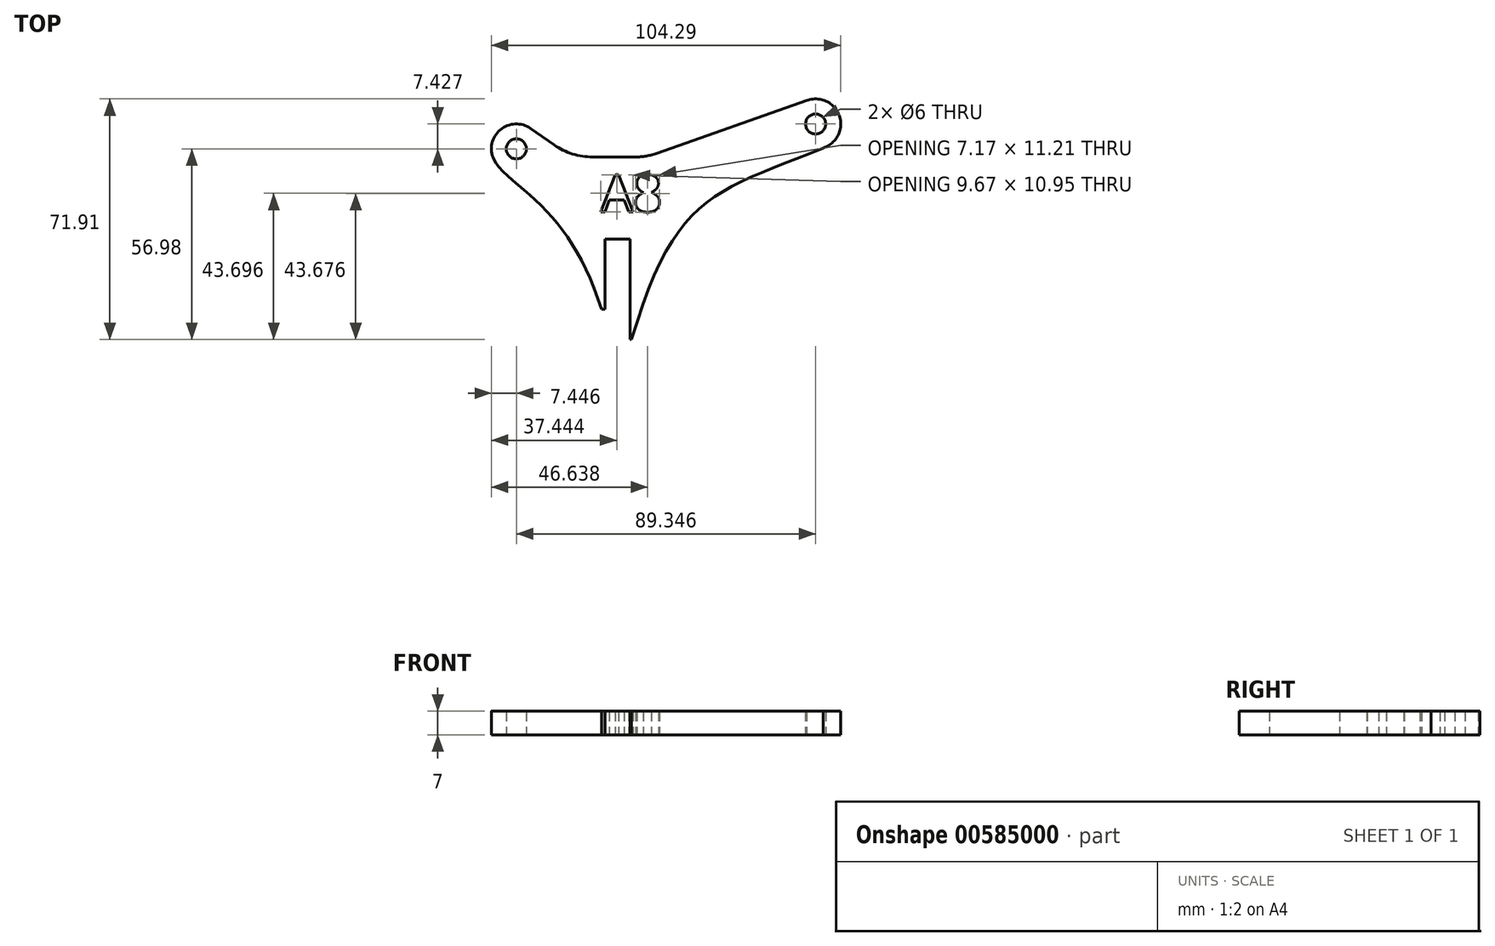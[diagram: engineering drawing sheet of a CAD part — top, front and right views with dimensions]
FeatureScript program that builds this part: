
annotation { "Feature Type Name" : "Feature", "Feature Type Description" : "" }
export const myFeature = defineFeature(function(context is Context, id is Id, definition is map)
    precondition{}
    {
        {
            var Q0;
            Q0=qCreatedBy(makeId("Top.planeOp"),FACE);
            var sketch = newSketch(context, id + "F0", { "sketchPlane" : qUnion([Q0])});
            skLineSegment(sketch, "E0", {"start": v(-34.62, 42.23) * mm, "end": v(65.38, 42.2) * mm, "construction": true});
            skLineSegment(sketch, "E1.left", {"start": v(2.5, -5) * mm, "end": v(2.5, 7.8) * mm});
            skLineSegment(sketch, "E1.right", {"start": v(10, -15) * mm, "end": v(10, 7.8) * mm});
            skPoint(sketch, "E1.middle", {"position": v(0, 0) * mm});
            skArc(sketch, "E2", {"start": v(67.67, 35.06) * mm, "mid": v(72.45, 44.7) * mm, "end": v(62.67, 49.2) * mm});
            skLineSegment(sketch, "E3", {"start": v(-34.62, 42.23) * mm, "end": v(15.38, 42.22) * mm, "construction": true});
            skLineSegment(sketch, "E4", {"start": v(-19.7, 40.88) * mm, "end": v(-12.67, 35.97) * mm});
            skLineSegment(sketch, "E5", {"start": v(18.13, 33.5) * mm, "end": v(62.67, 49.2) * mm});
            skLineSegment(sketch, "E6", {"start": v(-1.21, 32.36) * mm, "end": v(11.48, 32.36) * mm});
            skPoint(sketch, "E7.orphan", {"position": v(0, 27.1) * mm});
            skLineSegment(sketch, "E8", {"start": v(15.38, 42.22) * mm, "end": v(15.38, 24.58) * mm, "construction": true});
            skLineSegment(sketch, "E9", {"start": v(-34.62, 42.23) * mm, "end": v(-1.08, 18.78) * mm, "construction": true});
            skLineSegment(sketch, "E10", {"start": v(65.38, 42.2) * mm, "end": v(-1.08, 18.78) * mm, "construction": true});
            skCircle(sketch, "E11", {"center": v(65.38, 42.2) * mm, "radius": 3 * mm});
            skCircle(sketch, "E12", {"center": v(-23.96, 34.78) * mm, "radius": 3 * mm});
            skLineSegment(sketch, "E13", {"start": v(-23.96, 34.78) * mm, "end": v(90.1, 34.76) * mm, "construction": true});
            skLineSegment(sketch, "E14", {"start": v(-13.3, 27.33) * mm, "end": v(81.32, 27.31) * mm, "construction": true});
            skLineSegment(sketch, "E15", {"start": v(2.5, 7.8) * mm, "end": v(10, 7.8) * mm});
            skLineSegment(sketch, "E16", {"start": v(2.5, -5) * mm, "end": v(2.5, -13.17) * mm});
            skLineSegment(sketch, "E17", {"start": v(10, -15) * mm, "end": v(10, -22.2) * mm});
            skFitSpline(sketch, "E18", {"points": [v(10, -23.7) * mm, v(67.67, 35.06) * mm], "startDerivative": vector(38.94, 135.29) * mm, "endDerivative": vector(98.1, 40.08) * mm});
            skText(sketch, "E19", { "text": "A8", "fontName": "OpenSans-Regular.ttf"});
            skArc(sketch, "E20", {"start": v(-19.7, 40.88) * mm, "mid": v(-28.76, 40.47) * mm, "end": v(-30.7, 31.6) * mm});
            skPoint(sketch, "E21.0.visualSharp", {"position": v(-7.51, 32.36) * mm});
            skArc(sketch, "E21.0.filletArc", {"start": v(-12.67, 35.97) * mm, "mid": v(-7.22, 33.28) * mm, "end": v(-1.21, 32.36) * mm});
            skPoint(sketch, "E22.0.visualSharp", {"position": v(14.9, 32.36) * mm});
            skArc(sketch, "E22.0.filletArc", {"start": v(11.48, 32.36) * mm, "mid": v(14.85, 32.65) * mm, "end": v(18.13, 33.5) * mm});
            skLineSegment(sketch, "E23", {"start": v(2.5, -13.17) * mm, "end": v(1.5, -13.17) * mm});
            skLineSegment(sketch, "E24", {"start": v(10, -22.2) * mm, "end": v(10.44, -22.2) * mm});
            skFitSpline(sketch, "E25", {"points": [v(1.5, -13.17) * mm, v(-17.31, 18.56) * mm, v(-30.7, 31.6) * mm], "startDerivative": vector(-25.05, 77.18) * mm, "endDerivative": vector(-12.43, 26.26) * mm});
            const initialGuessF0  = {"E19": [0.0012, 0.01602, 1, 0, 0.011]};
            skSetInitialGuess(sketch, initialGuessF0);
            skSolve(sketch);
        }
        {
            var Q0;
            Q0=makeQuery(id+"F0.imprint","IMPRINT",FACE,{"disambiguationData":[TD([[makeQuery(id+"F0.imprint","IMPRINT",EDGE,{"derivedFrom":sQuery(id+"F0.wireOp",EDGE,"E1.top")}),1.0]])]});
            var Q1;
            Q1=makeQuery(id+"F0.imprint","IMPRINT",FACE,{"disambiguationData":[TD([[makeQuery(id+"F0.imprint","IMPRINT",EDGE,{"derivedFrom":sQuery(id+"F0.wireOp",EDGE,"E1.left")}),1.0]])]});
            extrude(context, id + "F1", {"entities" : qUnion([Q0, Q1]), "depth" : 7 * mm, "offsetDistance" : 25 * mm});
        }
    });
